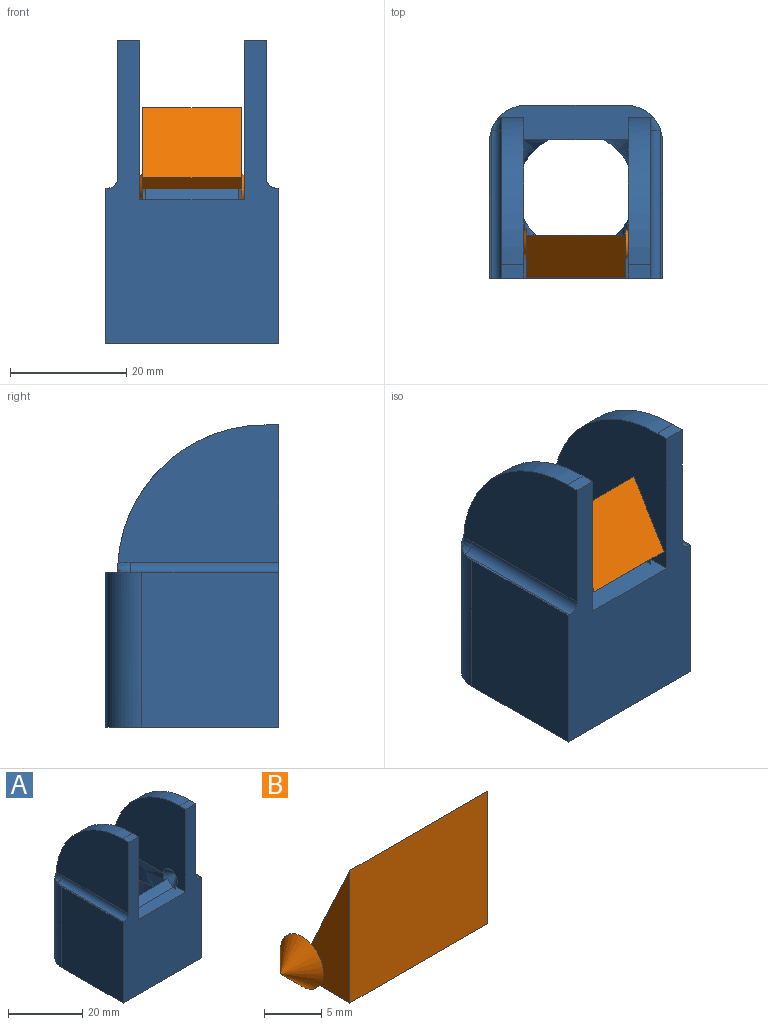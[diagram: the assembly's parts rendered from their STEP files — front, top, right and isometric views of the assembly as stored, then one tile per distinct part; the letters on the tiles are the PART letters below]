
ASSEMBLY  parts=2 mates=1
PART A: 36 faces, bbox 30x30x52.2 mm
  f0: plane 52.07x29.85mm, normal (0,-1,0), area 955.1mm2, adj f7,f9,f10,f11,f14,f16,f18,f19
  f1: cone r=2.67mm half-angle=45deg, axis (1,0,0), area 38mm2, adj f2,f5,f8,f21,f32,f33
  f2: plane 3.98x3.76mm, normal (-1,0,0), area 7mm2, adj f1,f5,f32,f34
  f3: cone r=2.67mm half-angle=45deg, axis (-1,0,0), area 38mm2, adj f4,f5,f6,f7,f32,f35
  f4: plane 3.98x3.76mm, normal (1,0,0), area 7mm2, adj f3,f5,f32,f34
  f5: bspline ~18.01x7.62mm, area 124.2mm2, adj f1,f2,f3,f4,f6,f8,f12,f34
  f6: bspline ~18.01x7.62mm, area 124mm2, adj f3,f5,f7,f12,f23
  f7: plane 27.74x27.38mm, normal (-1,0,0), area 561.9mm2, adj f0,f3,f6,f13,f22,f27,f32,f35
  f8: bspline ~18.01x7.62mm, area 124mm2, adj f1,f5,f12,f21,f23
  f9: plane 25.58x0.33mm, normal (0,0,1), area 8.2mm2, adj f0,f16,f25,f28
  f10: plane 25.58x0.33mm, normal (0,0,1), area 8.2mm2, adj f0,f14,f24,f30
  f11: plane 3.81x2.34mm, normal (0,0,1), area 8.9mm2, adj f0,f20,f21,f26
  f12: plane 27.31x27.31mm, normal (0,0,-1), area 261.3mm2, adj f5,f6,f8,f17,f23
  f13: plane 26.68x5.92mm, normal (0,0,1), area 118.8mm2, adj f7,f15,f21,f23,f24,f25,f26,f27
  f14: plane 26.67x23.57mm, normal (1,0,0), area 628.6mm2, adj f0,f10,f18,f24
  f15: plane 26.67x17.3mm, normal (0,1,0), area 461.3mm2, adj f13,f18,f24,f25
  f16: plane 26.67x23.57mm, normal (-1,0,0), area 628.6mm2, adj f0,f9,f18,f25
  f17: cylinder r=13.65mm len=27.31mm, axis (0,0,1), area 1634.1mm2, adj f12,f18
  f18: plane 29.85x29.85mm, normal (0,0,-1), area 288.3mm2, adj f0,f14,f15,f16,f17,f24,f25
  f19: plane 27.7x23.91mm, normal (1,0,0), area 516.9mm2, adj f0,f22,f27,f30,f31
  f20: plane 27.69x23.9mm, normal (-1,0,0), area 516.9mm2, adj f0,f11,f26,f28,f29
  f21: plane 27.74x27.38mm, normal (1,0,0), area 561.9mm2, adj f0,f1,f8,f11,f13,f26,f32,f33
  f22: plane 3.81x2.34mm, normal (0,0,1), area 8.9mm2, adj f0,f7,f19,f27
  f23: bspline ~18.01x7.62mm, area 128.4mm2, adj f6,f8,f12,f13
  f24: cylinder r=6.27mm len=26.67mm, axis (0,0,-1), area 262.8mm2, adj f10,f13,f14,f15,f18,f31
  f25: cylinder r=6.27mm len=26.67mm, axis (0,0,1), area 262.8mm2, adj f9,f13,f15,f16,f18,f29
  f26: cylinder r=25.4mm len=25.4mm, axis (1,0,0), area 152.4mm2, adj f11,f13,f20,f21,f29
  f27: cylinder r=25.4mm len=25.4mm, axis (1,0,0), area 152.4mm2, adj f7,f13,f19,f22,f31
  f28: cylinder r=1.78mm len=25.58mm, axis (0,-1,0), area 71.4mm2, adj f0,f9,f20,f29
  f29: bspline ~4.02x1.95mm, area 5.4mm2, adj f20,f25,f26,f28
  f30: cylinder r=1.78mm len=25.58mm, axis (0,1,0), area 71.4mm2, adj f0,f10,f19,f31
  f31: bspline ~3.27x1.78mm, area 5.1mm2, adj f19,f24,f27,f30
  f32: plane 18.12x4.05mm, normal (0,0,1), area 69.8mm2, adj f0,f1,f2,f3,f4,f7,f21,f33
  f33: plane 0.14x0.1mm, normal (0,-0.71,0.71), area 0mm2, adj f1,f21,f32
  f34: plane 15.98x1.98mm, normal (0,-0.71,0.71), area 44.8mm2, adj f2,f4,f5,f32
  f35: plane 0.14x0.1mm, normal (0,-0.71,0.71), area 0mm2, adj f3,f7,f32
PART B: 12 faces, bbox 22.3x8.6x15.4 mm
  f0: plane 5.33x4.89mm, normal (-1,0,0), area 16.9mm2, adj f1,f6,f7,f11
  f1: cone r=2.67mm half-angle=45deg, axis (-1,0,0), area 31.5mm2, adj f0,f9,f11
  f2: plane 5.33x4.89mm, normal (1,0,0), area 16.9mm2, adj f3,f6,f7,f10
  f3: cone r=2.67mm half-angle=45deg, axis (1,0,0), area 31.5mm2, adj f2,f4,f10
  f4: plane 14.17x4.79mm, normal (-1,0,0), area 38.5mm2, adj f3,f5,f6,f8
  f5: plane 16.99x14.17mm, normal (0,-1,0), area 240.7mm2, adj f4,f6,f8,f9
  f6: plane 16.99x12.18mm, normal (0,0.91,0.42), area 228.4mm2, adj f0,f2,f4,f5,f7,f9
  f7: plane 16.99x1.98mm, normal (0,0.71,-0.71), area 47.7mm2, adj f0,f2,f6,f8
  f8: plane 16.99x3.7mm, normal (0,0,-1), area 62.8mm2, adj f4,f5,f7,f9
  f9: plane 14.17x4.79mm, normal (1,0,0), area 38.5mm2, adj f1,f5,f6,f8
  f10: plane 0.75x0.75mm, normal (0,-0.71,-0.71), area 0mm2, adj f2,f3
  f11: plane 0.75x0.75mm, normal (0,-0.71,-0.71), area 0mm2, adj f0,f1
PLACE A at identity fixed
PLACE B rot(axis=(-1,0,0),31.3deg) t=(0,-5.26,-3.57)mm
MATE revolute A.f1 <-> B.f3  axis (-1,0,0) through (9,-9,7.62)mm
